# Revit family: NLRS_00_GM_Geluiddempend muurrooster_ST-448-300_Storax
name_source: partatom
category: Generic Models
units: mm (PartAtom-declared; Revit-internal decimal feet)

## family parameters
Always vertical = No
Can host rebar = No
Cut with Voids When Loaded = Yes
Part Type = Normal
Room Calculation Point = No
Round Connector Dimension = Use Diameter
Shared = No
Work Plane-Based = Yes

## types (1)
- NLRS_00_GM_Geluiddempend muurrooster_ST-448-300_Storax
    Blade Offset Bottom = 11 mm  [stored 0.0360892 ft]
    Blade Spacing = 150 mm
    Default Elevation = 1219 mm
    Rooster End = 14 mm  [stored 0.0459318 ft]
    Rooster Start = 14 mm  [stored 0.0459318 ft]
    Thickness = 7 mm  [stored 0.0229659 ft]
    Thickness wall = 505 mm  [stored 1.65682 ft]
    Type Comments = ST-445-86

note: [stored X ft] marks values corroborated as IEEE doubles in the binary element streams (Revit-internal decimal feet)

## geometry (parser evidence)
native form markers: Sweep x26
no freeform markers — native parametric forms only
